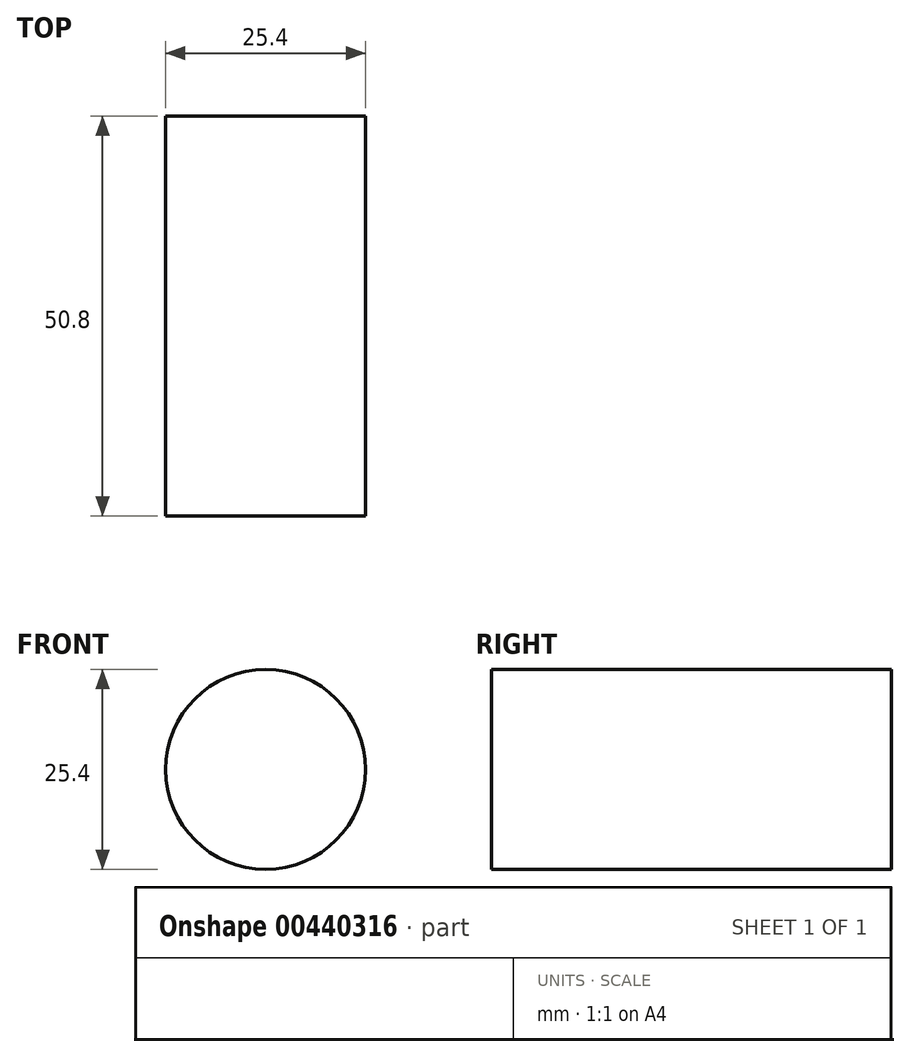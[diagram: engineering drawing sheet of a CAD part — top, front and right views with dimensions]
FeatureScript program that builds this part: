
annotation { "Feature Type Name" : "Feature", "Feature Type Description" : "" }
export const myFeature = defineFeature(function(context is Context, id is Id, definition is map)
    precondition{}
    {
        {
            var Q0;
            Q0=qCreatedBy(makeId("Front.planeOp"),FACE);
            var sketch = newSketch(context, id + "F0", { "sketchPlane" : qUnion([Q0])});
            skCircle(sketch, "E0", {"center": v(-13.37, 3.54) * mm, "radius": 12.7 * mm});
            skSolve(sketch);
        }
        {
            var Q0;
            Q0 = qSketchRegion(id + "F0", true);
            extrude(context, id + "F1", {"entities" : qUnion([Q0]), "depth" : 50.8 * mm});
        }
    });
